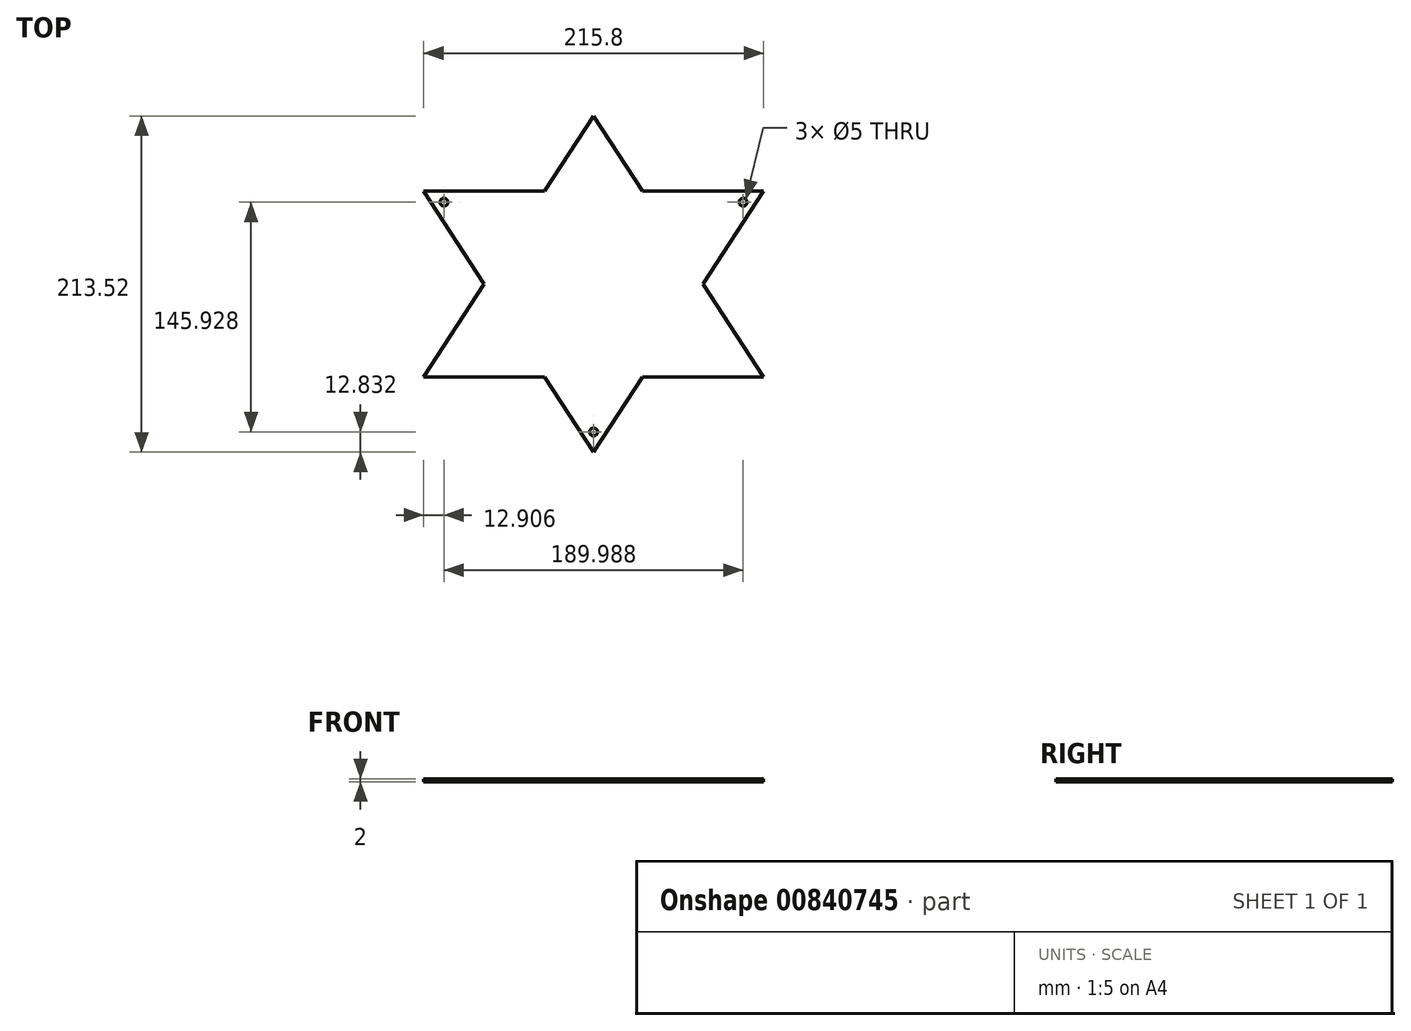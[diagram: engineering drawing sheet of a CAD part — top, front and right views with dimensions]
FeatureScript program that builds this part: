
annotation { "Feature Type Name" : "Feature", "Feature Type Description" : "" }
export const myFeature = defineFeature(function(context is Context, id is Id, definition is map)
    precondition{}
    {
        {
            var Q0;
            Q0=qCreatedBy(makeId("Top.planeOp"),FACE);
            var sketch = newSketch(context, id + "F0", { "sketchPlane" : qUnion([Q0])});
            skLineSegment(sketch, "E0", {"start": v(0, 91.12) * mm, "end": v(-107.9, -74.64) * mm});
            skLineSegment(sketch, "E1", {"start": v(-107.9, -74.64) * mm, "end": v(107.9, -74.64) * mm});
            skLineSegment(sketch, "E2", {"start": v(107.9, -74.64) * mm, "end": v(0, 91.12) * mm});
            skLineSegment(sketch, "E3", {"start": v(-107.9, 43.36) * mm, "end": v(107.9, 43.36) * mm});
            skLineSegment(sketch, "E4", {"start": v(107.9, 43.36) * mm, "end": v(0, -122.4) * mm});
            skLineSegment(sketch, "E5", {"start": v(-107.9, 43.36) * mm, "end": v(0, -122.4) * mm});
            skCircle(sketch, "E6", {"center": v(-95, 36.36) * mm, "radius": 2.5 * mm});
            skCircle(sketch, "E7", {"center": v(95, 36.36) * mm, "radius": 2.5 * mm});
            skCircle(sketch, "E8", {"center": v(0, -109.57) * mm, "radius": 2.5 * mm});
            skSolve(sketch);
        }
        {
            var Q0;
            {var subQ0=sQuery(id+"F0.wireOp",EDGE,"E3");var subQ1=sQuery(id+"F0.wireOp",EDGE,"E0");var subQ2=makeQuery(id+"F0.imprint","INTERSECT",VERTEX,{"derivedFrom":[subQ1,subQ0]});Q0=makeQuery(id+"F0.imprint","IMPRINT",FACE,{"disambiguationData":[TD([[makeQuery(id+"F0.imprint","IMPRINT",EDGE,{"disambiguationData":[TD([[subQ2,-1.0]])],"derivedFrom":subQ1}),1.0]])]});}
            var Q1;
            Q1=makeQuery(id+"F0.imprint","IMPRINT",FACE,{"disambiguationData":[TD([[makeQuery(id+"F0.imprint","IMPRINT",EDGE,{"derivedFrom":sQuery(id+"F0.wireOp",EDGE,"E6")}),-1.0]])]});
            var Q2;
            Q2=makeQuery(id+"F0.imprint","IMPRINT",FACE,{"disambiguationData":[TD([[makeQuery(id+"F0.imprint","IMPRINT",EDGE,{"derivedFrom":sQuery(id+"F0.wireOp",EDGE,"E7")}),-1.0]])]});
            var Q3;
            {var subQ0=sQuery(id+"F0.wireOp",EDGE,"E2");var subQ1=sQuery(id+"F0.wireOp",EDGE,"E0");var subQ2=makeQuery(id+"F0.imprint","INTERSECT",VERTEX,{"derivedFrom":[subQ1,subQ0]});Q3=makeQuery(id+"F0.imprint","IMPRINT",FACE,{"disambiguationData":[TD([[makeQuery(id+"F0.imprint","IMPRINT",EDGE,{"disambiguationData":[TD([[subQ2,-1.0]])],"derivedFrom":subQ1}),1.0]])]});}
            var Q4;
            {var subQ0=sQuery(id+"F0.wireOp",EDGE,"E2");var subQ1=sQuery(id+"F0.wireOp",EDGE,"E1");var subQ2=makeQuery(id+"F0.imprint","INTERSECT",VERTEX,{"derivedFrom":[subQ1,subQ0]});Q4=makeQuery(id+"F0.imprint","IMPRINT",FACE,{"disambiguationData":[TD([[makeQuery(id+"F0.imprint","IMPRINT",EDGE,{"disambiguationData":[TD([[subQ2,1.0]])],"derivedFrom":subQ1}),1.0]])]});}
            var Q5;
            Q5=makeQuery(id+"F0.imprint","IMPRINT",FACE,{"disambiguationData":[TD([[makeQuery(id+"F0.imprint","IMPRINT",EDGE,{"derivedFrom":sQuery(id+"F0.wireOp",EDGE,"E8")}),-1.0]])]});
            var Q6;
            {var subQ0=sQuery(id+"F0.wireOp",EDGE,"E1");var subQ1=sQuery(id+"F0.wireOp",EDGE,"E0");var subQ2=makeQuery(id+"F0.imprint","INTERSECT",VERTEX,{"derivedFrom":[subQ1,subQ0]});Q6=makeQuery(id+"F0.imprint","IMPRINT",FACE,{"disambiguationData":[TD([[makeQuery(id+"F0.imprint","IMPRINT",EDGE,{"disambiguationData":[TD([[subQ2,1.0]])],"derivedFrom":subQ1}),1.0]])]});}
            extrude(context, id + "F1", {"entities" : qUnion([Q0, Q1, Q2, Q3, Q4, Q5, Q6]), "depth" : 2 * mm, "offsetDistance" : 25 * mm});
        }
    });
